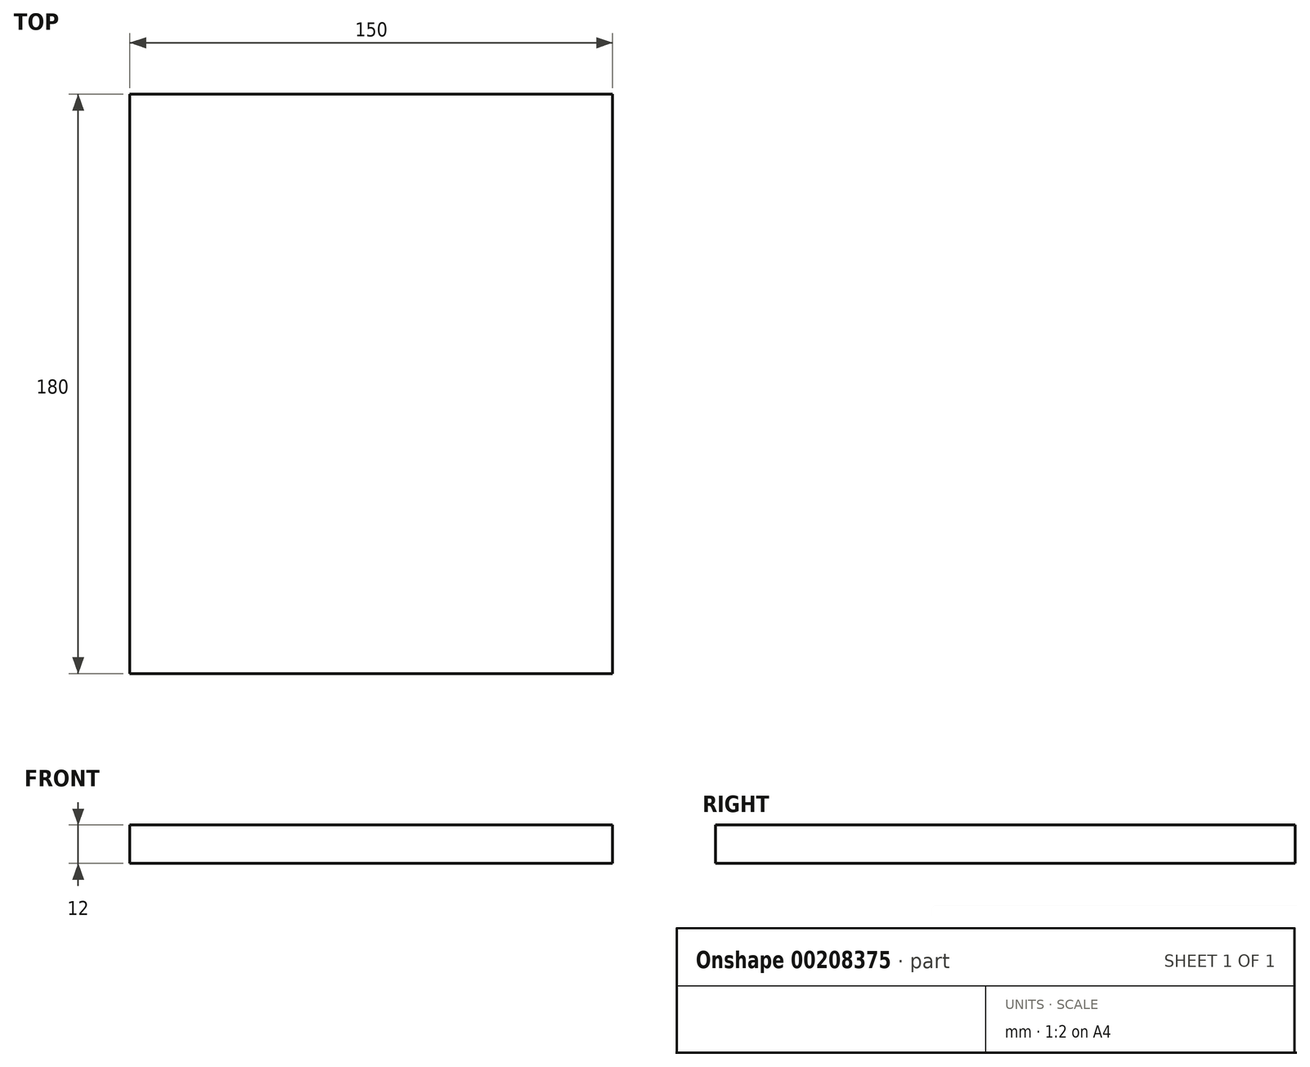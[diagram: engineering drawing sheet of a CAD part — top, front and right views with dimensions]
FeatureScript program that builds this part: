
annotation { "Feature Type Name" : "Feature", "Feature Type Description" : "" }
export const myFeature = defineFeature(function(context is Context, id is Id, definition is map)
    precondition{}
    {
        {
            var Q0;
            Q0=qCreatedBy(makeId("Top.planeOp"),FACE);
            var sketch = newSketch(context, id + "F1", { "sketchPlane" : qUnion([Q0])});
            skLineSegment(sketch, "E0.bottom", {"start": v(-75.89, 93.02) * mm, "end": v(74.11, 93.02) * mm});
            skLineSegment(sketch, "E0.top", {"start": v(-75.89, -86.98) * mm, "end": v(74.11, -86.98) * mm});
            skLineSegment(sketch, "E0.left", {"start": v(-75.89, 93.02) * mm, "end": v(-75.89, -86.98) * mm});
            skLineSegment(sketch, "E0.right", {"start": v(74.11, 93.02) * mm, "end": v(74.11, -86.98) * mm});
            skSolve(sketch);
        }
        {
            var Q0;
            Q0=makeQuery(id+"F1.imprint","IMPRINT",FACE,{"disambiguationData":[TD([[makeQuery(id+"F1.imprint","IMPRINT",EDGE,{"derivedFrom":sQuery(id+"F1.wireOp",EDGE,"E0.bottom")}),-1.0]])]});
            extrude(context, id + "F0", {"entities" : qUnion([Q0]), "depth" : 12 * mm});
        }
    });
